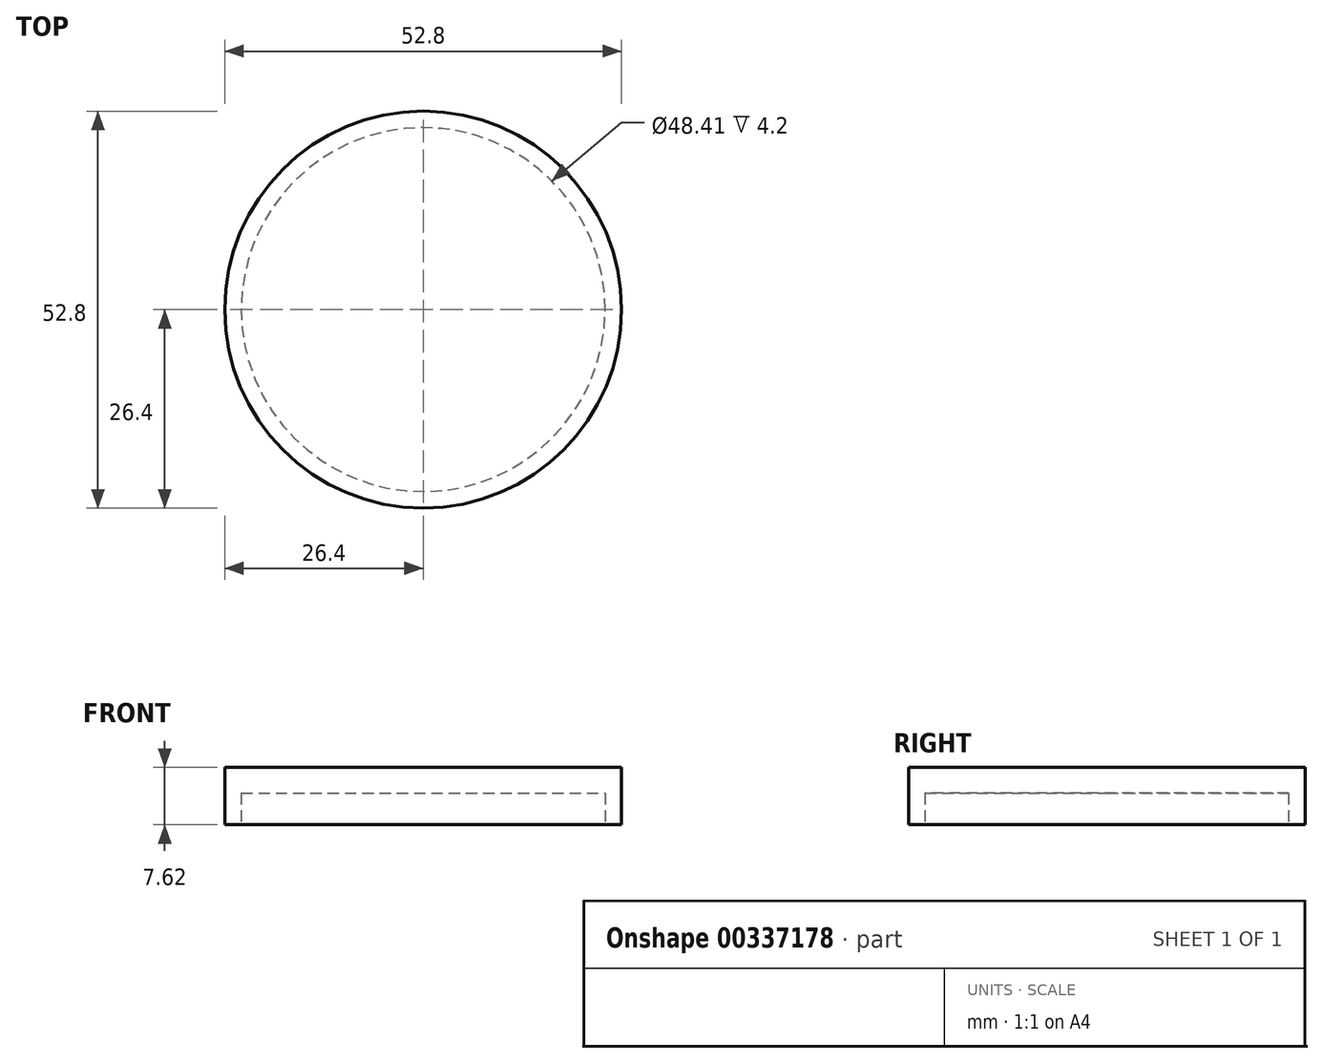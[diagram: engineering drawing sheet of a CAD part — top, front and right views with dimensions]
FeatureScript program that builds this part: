
annotation { "Feature Type Name" : "Feature", "Feature Type Description" : "" }
export const myFeature = defineFeature(function(context is Context, id is Id, definition is map)
    precondition{}
    {
        {
            var Q0;
            Q0=qCreatedBy(makeId("Top.planeOp"),FACE);
            var sketch = newSketch(context, id + "F0", { "sketchPlane" : qUnion([Q0])});
            skCircle(sketch, "E0", {"center": v(0, 0) * mm, "radius": 26.4 * mm});
            skSolve(sketch);
        }
        {
            var Q0;
            Q0=makeQuery(id+"F0.imprint","IMPRINT",FACE,{"disambiguationData":[TD([[makeQuery(id+"F0.imprint","IMPRINT",EDGE,{"derivedFrom":sQuery(id+"F0.wireOp",EDGE,"E0")}),1.0]])]});
            extrude(context, id + "F1", {"entities" : qUnion([Q0]), "oppositeDirection" : true, "depth" : 7.62 * mm});
        }
        {
            var Q0;
            Q0=makeQuery(id+"F1.opExtrude","CAP_FACE",FACE,{"disambiguationData":[OSD([sQuery(id+"F0.wireOp",EDGE,"E0")])],"isStart":false});
            var sketch = newSketch(context, id + "F2", { "sketchPlane" : qUnion([Q0])});
            skCircle(sketch, "E1", {"center": v(0, 0) * mm, "radius": 24.2 * mm});
            skSolve(sketch);
        }
        {
            var Q0;
            Q0 = qSketchRegion(id + "F2", true);
            extrude(context, id + "F3", {"entities" : qUnion([Q0]), "operationType" : NewBodyOperationType.REMOVE, "oppositeDirection" : true, "depth" : 4.2 * mm});
        }
    });
